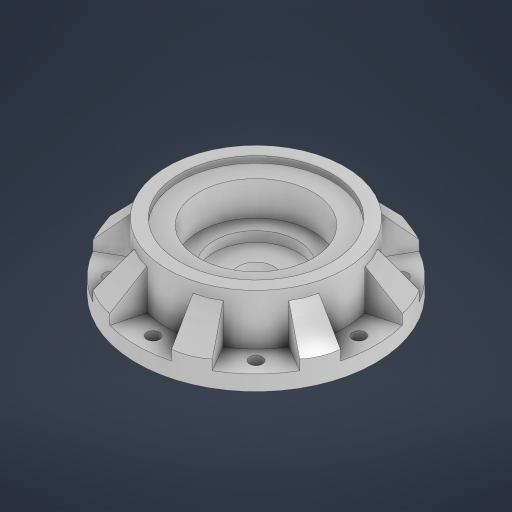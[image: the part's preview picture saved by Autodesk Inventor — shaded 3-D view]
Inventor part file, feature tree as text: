
AUTODESK INVENTOR PART (.ipt)
format: ipt  version: 2024 (Build 280153000, 153)  size: 513,536 bytes
history: native  units: mm
features: extrude x9, sketch x9, pattern_circular x2, chamfer x1, projected_geometry x1
ambient origin geometry x8: Origin, YZ Plane, XZ Plane, XY Plane, X Axis, Y Axis, Z Axis, Center Point
bodies: Solid1 (feature_tree)
feature tree (22):
  extrude  "Extrusion1"  Depth=12.0mm TaperAngle=0.0deg
  extrude  "Extrusion2"  Depth=10.0mm TaperAngle=0.0deg
  extrude  "Extrusion3"  Depth=90.0mm
  pattern_circular  "Circular Pattern1"  Count=14  [1 undecoded]
  extrude  "Extrusion4"  Depth=5.0mm TaperAngle=0.0deg
  extrude  "Extrusion5"  Depth=80.0mm TaperAngle=360.0deg
  extrude  "Extrusion6"  TaperAngle=15.0deg  [1 undecoded]
  extrude  "Extrusion7"  Depth=1.308997mm
  extrude  "Extrusion8"  Depth=31.5mm TaperAngle=0.0deg
  chamfer  "Chamfer1"  Distance=31.5mm Angle=45.0deg
  pattern_circular  "Circular Pattern2"  Count=8 Angle=360.0deg
  extrude  "Extrusion10"  [1 undecoded]
  sketch  "Sketch1"  dims[d0=250.0mm d1=12.0mm d2=0.0mm]
  sketch  "Sketch2"  dims[d3=40.0mm d4=0.0mm d5=10.0mm d6=0.0mm]
  projected_geometry  "Projected Loop1"
  sketch  "Sketch3"  dims[d7=1800.0mm d8=360.0deg d10=90.0mm d11=140.0mm]
  sketch  "Sketch4"  dims[d12=8.0mm d13=0.0mm d14=5.0mm d15=0.0mm]
  sketch  "Sketch5"  dims[d16=25.0mm d17=0.0mm d18=80.0mm d20=360.0deg]
  sketch  "Sketch6"  dims[d22=20.0mm d23=0.0mm d24=15.0deg]
  sketch  "Sketch7"  dims[d25=60.0deg d26=1.308997mm]
  sketch  "Sketch8"  dims[d27=1.308997mm d28=31.5mm d29=0.0mm d30=31.5mm d31=2.0mm d32=45.0deg d33=80.0mm d34=360.0deg]
  sketch  "Sketch10"  dims[d38=100.0mm d39=0.0mm]
note: 3 required parameter values undecoded (feature->parameter linkage not recoverable at this tier; creation-order binding heuristic only, values carry confidence <= 0.55)
